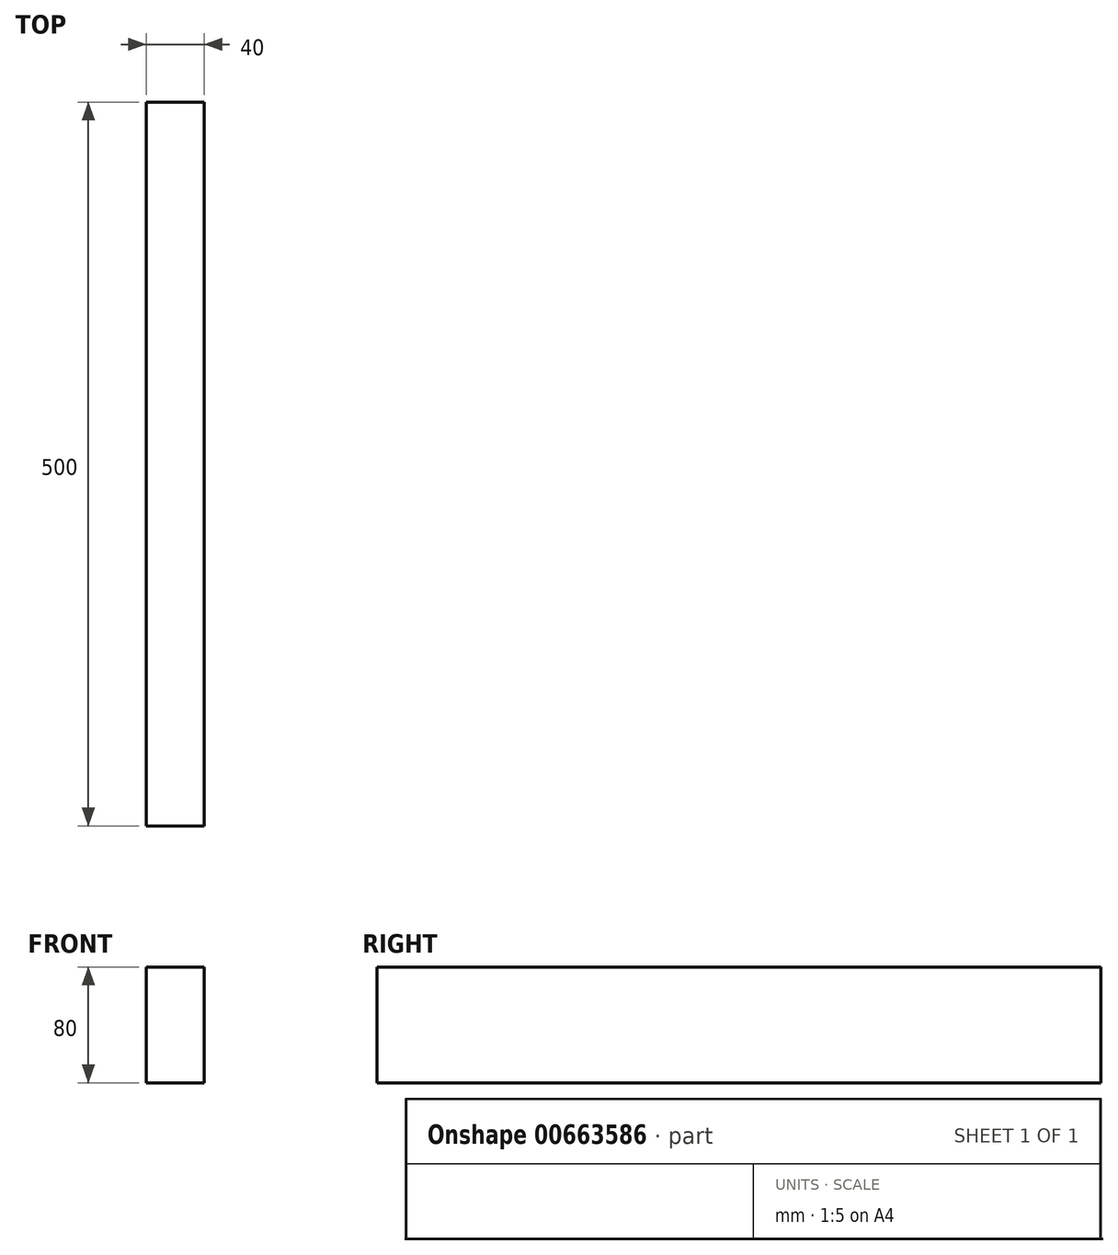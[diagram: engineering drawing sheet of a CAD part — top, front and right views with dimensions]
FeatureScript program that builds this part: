
annotation { "Feature Type Name" : "Feature", "Feature Type Description" : "" }
export const myFeature = defineFeature(function(context is Context, id is Id, definition is map)
    precondition{}
    {
        {
            var Q0;
            Q0=qCreatedBy(makeId("Front.planeOp"),FACE);
            var sketch = newSketch(context, id + "F0", { "sketchPlane" : qUnion([Q0])});
            skLineSegment(sketch, "E0.bottom", {"start": v(20, 40) * mm, "end": v(-20, 40) * mm});
            skLineSegment(sketch, "E0.top", {"start": v(20, -40) * mm, "end": v(-20, -40) * mm});
            skLineSegment(sketch, "E0.left", {"start": v(20, 40) * mm, "end": v(20, -40) * mm});
            skLineSegment(sketch, "E0.right", {"start": v(-20, 40) * mm, "end": v(-20, -40) * mm});
            skPoint(sketch, "E0.middle", {"position": v(0, 0) * mm});
            skSolve(sketch);
        }
        {
            var Q0;
            Q0=makeQuery(id+"F0.imprint","IMPRINT",FACE,{"disambiguationData":[TD([[makeQuery(id+"F0.imprint","IMPRINT",EDGE,{"derivedFrom":sQuery(id+"F0.wireOp",EDGE,"E0.bottom")}),1.0]])]});
            extrude(context, id + "F1", {"entities" : qUnion([Q0]), "depth" : 500 * mm, "offsetDistance" : 25 * mm});
        }
    });
